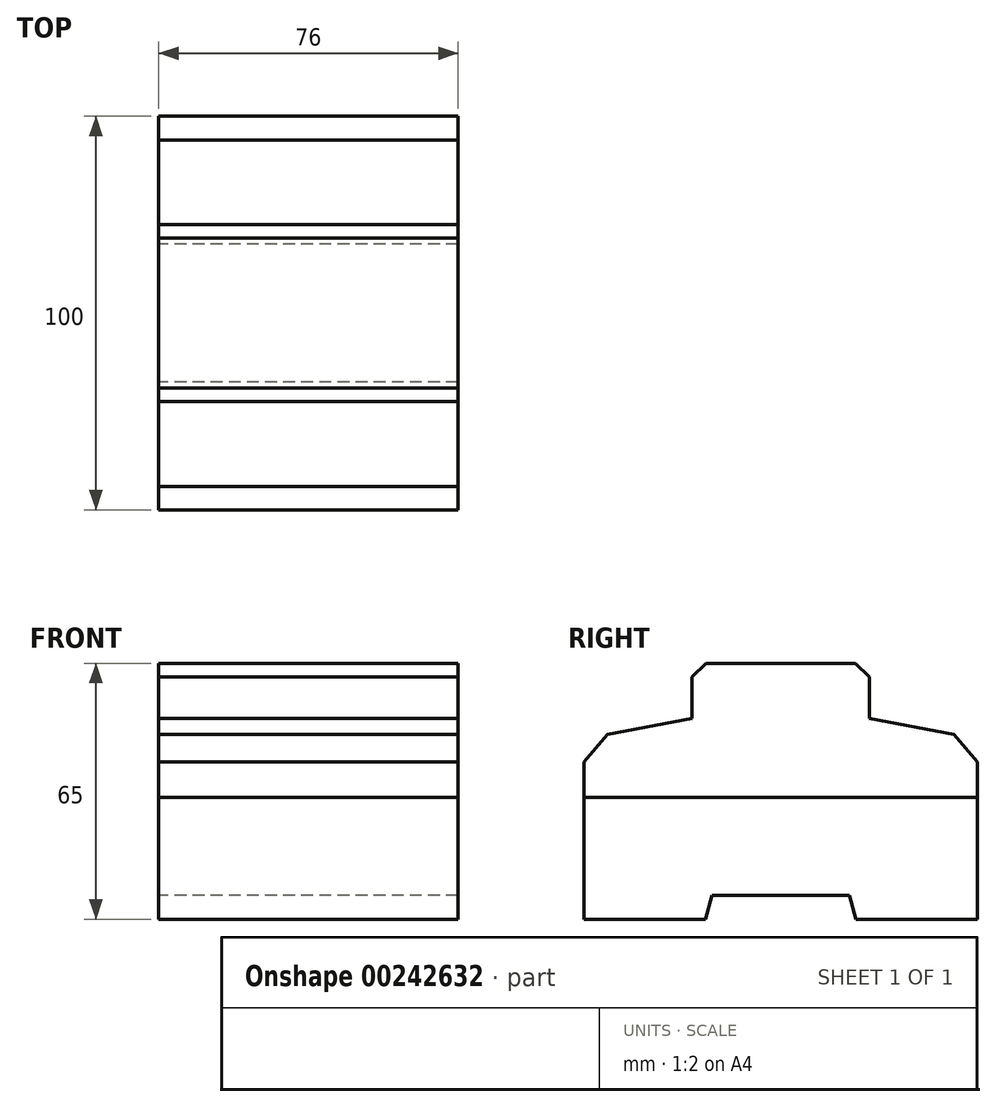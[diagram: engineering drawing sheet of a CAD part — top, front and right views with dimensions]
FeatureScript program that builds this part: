
annotation { "Feature Type Name" : "Feature", "Feature Type Description" : "" }
export const myFeature = defineFeature(function(context is Context, id is Id, definition is map)
    precondition{}
    {
        {
            var Q0;
            Q0=qCreatedBy(makeId("Right.planeOp"),FACE);
            var sketch = newSketch(context, id + "F0", { "sketchPlane" : qUnion([Q0])});
            skLineSegment(sketch, "E0", {"start": v(0, 0) * mm, "end": v(17.5, 0) * mm});
            skLineSegment(sketch, "E1", {"start": v(17.5, 0) * mm, "end": v(19.1, -6) * mm});
            skLineSegment(sketch, "E2", {"start": v(19.1, -6) * mm, "end": v(50, -6) * mm});
            skLineSegment(sketch, "E3", {"start": v(50, -6) * mm, "end": v(50, 25) * mm});
            skLineSegment(sketch, "E4", {"start": v(50, 25) * mm, "end": v(0, 25) * mm});
            skLineSegment(sketch, "E5.MirrorCS", {"start": v(-17.5, 0) * mm, "end": v(-19.1, -6) * mm});
            skLineSegment(sketch, "E6.MirrorCS", {"start": v(-19.1, -6) * mm, "end": v(-50, -6) * mm});
            skLineSegment(sketch, "E7.MirrorCS", {"start": v(-50, 25) * mm, "end": v(0, 25) * mm});
            skLineSegment(sketch, "E8.MirrorCS", {"start": v(0, 0) * mm, "end": v(-17.5, 0) * mm});
            skLineSegment(sketch, "E9.MirrorCS", {"start": v(-50, -6) * mm, "end": v(-50, 25) * mm});
            skSolve(sketch);
        }
        {
            var Q0;
            Q0 = qSketchRegion(id + "F0", true);
            extrude(context, id + "F1", {"entities" : qUnion([Q0]), "depth" : (76 / 2) * mm, "offsetDistance" : 25 * mm, "hasSecondDirection" : true, "secondDirectionOppositeDirection" : true, "secondDirectionDepth" : (76 / 2) * mm});
        }
        {
            var Q0;
            Q0=qCreatedBy(makeId("Right.planeOp"),FACE);
            var sketch = newSketch(context, id + "F2", { "sketchPlane" : qUnion([Q0])});
            skLineSegment(sketch, "E10.0", {"start": v(50, 25) * mm, "end": v(-50, 25) * mm});
            skLineSegment(sketch, "E11", {"start": v(-50, 25) * mm, "end": v(-50, 34) * mm});
            skLineSegment(sketch, "E12", {"start": v(-50, 34) * mm, "end": v(-44, 41) * mm});
            skLineSegment(sketch, "E13", {"start": v(-44, 41) * mm, "end": v(-22.5, 45) * mm});
            skLineSegment(sketch, "E14", {"start": v(-22.5, 45) * mm, "end": v(-22.5, 55.5) * mm});
            skLineSegment(sketch, "E15", {"start": v(-22.5, 55.5) * mm, "end": v(-19, 59) * mm});
            skLineSegment(sketch, "E16", {"start": v(-19, 59) * mm, "end": v(0, 59) * mm});
            skLineSegment(sketch, "E17.MirrorCS", {"start": v(22.5, 55.5) * mm, "end": v(19, 59) * mm});
            skLineSegment(sketch, "E18.MirrorCS", {"start": v(19, 59) * mm, "end": v(0, 59) * mm});
            skLineSegment(sketch, "E19.MirrorCS", {"start": v(50, 34) * mm, "end": v(44, 41) * mm});
            skLineSegment(sketch, "E20.MirrorCS", {"start": v(44, 41) * mm, "end": v(22.5, 45) * mm});
            skLineSegment(sketch, "E21.MirrorCS", {"start": v(22.5, 45) * mm, "end": v(22.5, 55.5) * mm});
            skLineSegment(sketch, "E22.MirrorCS", {"start": v(50, 25) * mm, "end": v(50, 34) * mm});
            skSolve(sketch);
        }
        {
            var Q0;
            Q0 = qSketchRegion(id + "F2", true);
            extrude(context, id + "F3", {"entities" : qUnion([Q0]), "depth" : (76 / 2) * mm, "offsetDistance" : 25 * mm, "hasSecondDirection" : true, "secondDirectionOppositeDirection" : true, "secondDirectionDepth" : (76 / 2) * mm});
        }
    });
